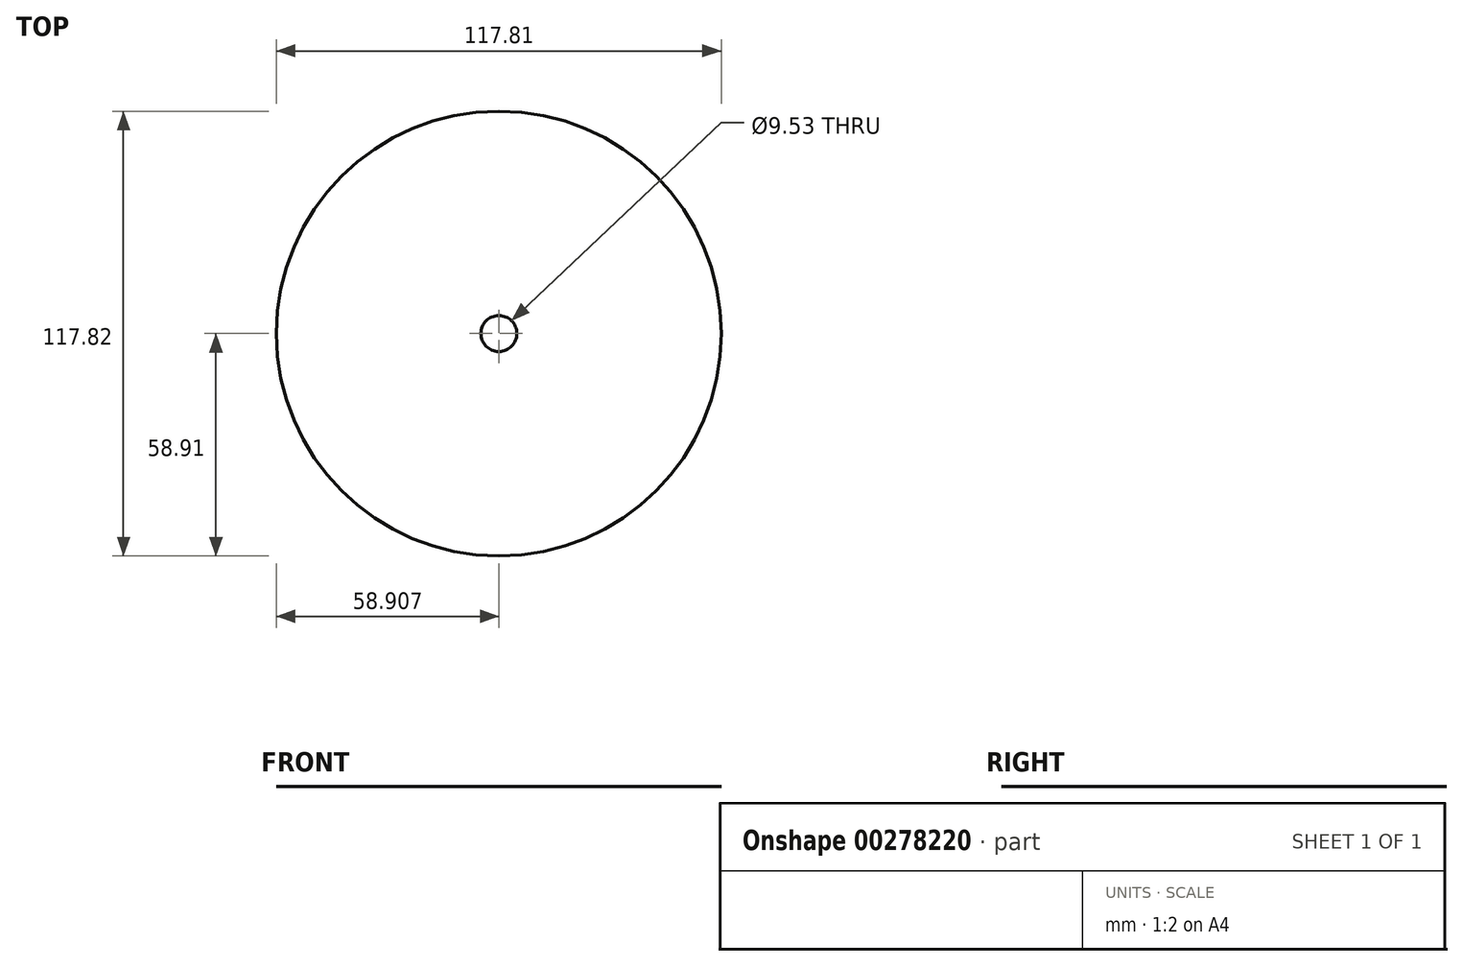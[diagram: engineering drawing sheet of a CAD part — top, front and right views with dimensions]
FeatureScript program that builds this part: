
annotation { "Feature Type Name" : "Feature", "Feature Type Description" : "" }
export const myFeature = defineFeature(function(context is Context, id is Id, definition is map)
    precondition{}
    {
        {
            var Q0;
            Q0=qCreatedBy(makeId("Top.planeOp"),FACE);
            var sketch = newSketch(context, id + "F0", { "sketchPlane" : qUnion([Q0])});
            skLineSegment(sketch, "E0", {"start": v(23.32, -31.1) * mm, "end": v(-63.12, -31.1) * mm});
            skLineSegment(sketch, "E1", {"start": v(-63.12, -31.1) * mm, "end": v(-6.56, 9.98) * mm});
            skCircle(sketch, "E2", {"center": v(23.32, -31.1) * mm, "radius": 58.9 * mm});
            skArc(sketch, "E3", {"start": v(2.15, -1.97) * mm, "mid": v(2.14, -1.98) * mm, "end": v(2.14, -1.98) * mm});
            skLineSegment(sketch, "E4", {"start": v(23.32, -31.1) * mm, "end": v(-12.69, -31.1) * mm});
            skLineSegment(sketch, "E5", {"start": v(-12.69, -31.1) * mm, "end": v(-12.69, 18.44) * mm});
            skCircle(sketch, "E6", {"center": v(-12.69, 18.44) * mm, "radius": 49.54 * mm});
            skArc(sketch, "E7.trimOffspring", {"start": v(-12.69, -31.1) * mm, "mid": v(44.48, -60.23) * mm, "end": v(34.43, 3.14) * mm});
            skCircle(sketch, "E8", {"center": v(23.32, -31.1) * mm, "radius": 4.76 * mm});
            skSolve(sketch);
        }
        {
            var Q0;
            {var subQ0=sQuery(id+"F0.wireOp",EDGE,"E6");var subQ5=sQuery(id+"F0.wireOp",EDGE,"E2");var subQ7=makeQuery(id+"F0.imprint","INTERSECT",VERTEX,{"disambiguationData":[OD(0.0)],"derivedFrom":[subQ5,subQ0]});Q0=makeQuery(id+"F0.imprint","IMPRINT",FACE,{"disambiguationData":[TD([[makeQuery(id+"F0.imprint","IMPRINT",EDGE,{"disambiguationData":[TD([[subQ7,-1.0]])],"derivedFrom":subQ5}),1.0]])]});}
            var Q1;
            {var subQ0=sQuery(id+"F0.wireOp",EDGE,"E7.trimOffspring");Q1=makeQuery(id+"F0.imprint","IMPRINT",FACE,{"disambiguationData":[TD([[makeQuery(id+"F0.imprint","IMPRINT",EDGE,{"derivedFrom":subQ0}),-1.0]])]});}
            var Q2;
            {var subQ0=sQuery(id+"F0.wireOp",EDGE,"E7.trimOffspring");Q2=makeQuery(id+"F0.imprint","IMPRINT",FACE,{"disambiguationData":[TD([[makeQuery(id+"F0.imprint","IMPRINT",EDGE,{"derivedFrom":subQ0}),1.0]])]});}
            var Q3;
            {var subQ0=sQuery(id+"F0.wireOp",EDGE,"E6");var subQ1=sQuery(id+"F0.wireOp",EDGE,"db185c22-ce6a-4d70-b337-dee1c4f94d18");var subQ2=makeQuery(id+"F0.imprint","INTERSECT",VERTEX,{"derivedFrom":[subQ1,subQ0]});Q3=makeQuery(id+"F0.imprint","IMPRINT",FACE,{"disambiguationData":[TD([[makeQuery(id+"F0.imprint","IMPRINT",EDGE,{"disambiguationData":[TD([[subQ2,-1.0]])],"derivedFrom":subQ1}),-1.0]])]});}
            var Q4;
            {var subQ0=sQuery(id+"F0.wireOp",EDGE,"E2");var subQ1=sQuery(id+"F0.wireOp",EDGE,"E1");var subQ2=makeQuery(id+"F0.imprint","INTERSECT",VERTEX,{"derivedFrom":[subQ1,subQ0]});Q4=makeQuery(id+"F0.imprint","IMPRINT",FACE,{"disambiguationData":[TD([[makeQuery(id+"F0.imprint","IMPRINT",EDGE,{"disambiguationData":[TD([[subQ2,-1.0]])],"derivedFrom":subQ1}),-1.0]])]});}
            var Q5;
            {var subQ1=sQuery(id+"F0.wireOp",EDGE,"E0");var subQ3=sQuery(id+"F0.wireOp",EDGE,"E2");var subQ4=makeQuery(id+"F0.imprint","INTERSECT",VERTEX,{"derivedFrom":[subQ1,subQ3]});Q5=makeQuery(id+"F0.imprint","IMPRINT",FACE,{"disambiguationData":[TD([[makeQuery(id+"F0.imprint","IMPRINT",EDGE,{"disambiguationData":[TD([[subQ4,1.0]])],"derivedFrom":subQ3}),1.0]])]});}
            var Q6;
            {var subQ0=sQuery(id+"F0.wireOp",EDGE,"E2");var subQ1=sQuery(id+"F0.wireOp",EDGE,"E1");var subQ2=makeQuery(id+"F0.imprint","INTERSECT",VERTEX,{"derivedFrom":[subQ1,subQ0]});Q6=makeQuery(id+"F0.imprint","IMPRINT",FACE,{"disambiguationData":[TD([[makeQuery(id+"F0.imprint","IMPRINT",EDGE,{"disambiguationData":[TD([[subQ2,-1.0]])],"derivedFrom":subQ1}),1.0]])]});}
            var Q7;
            {var subQ0=sQuery(id+"F0.wireOp",EDGE,"E3");Q7=makeQuery(id+"F0.imprint","IMPRINT",FACE,{"disambiguationData":[TD([[makeQuery(id+"F0.imprint","IMPRINT",EDGE,{"derivedFrom":subQ0}),-1.0]])]});}
            extrude(context, id + "F1", {"entities" : qUnion([Q0, Q1, Q2, Q3, Q4, Q5, Q6, Q7]), "depth" : 1 / 203.2 * mm});
        }
    });
